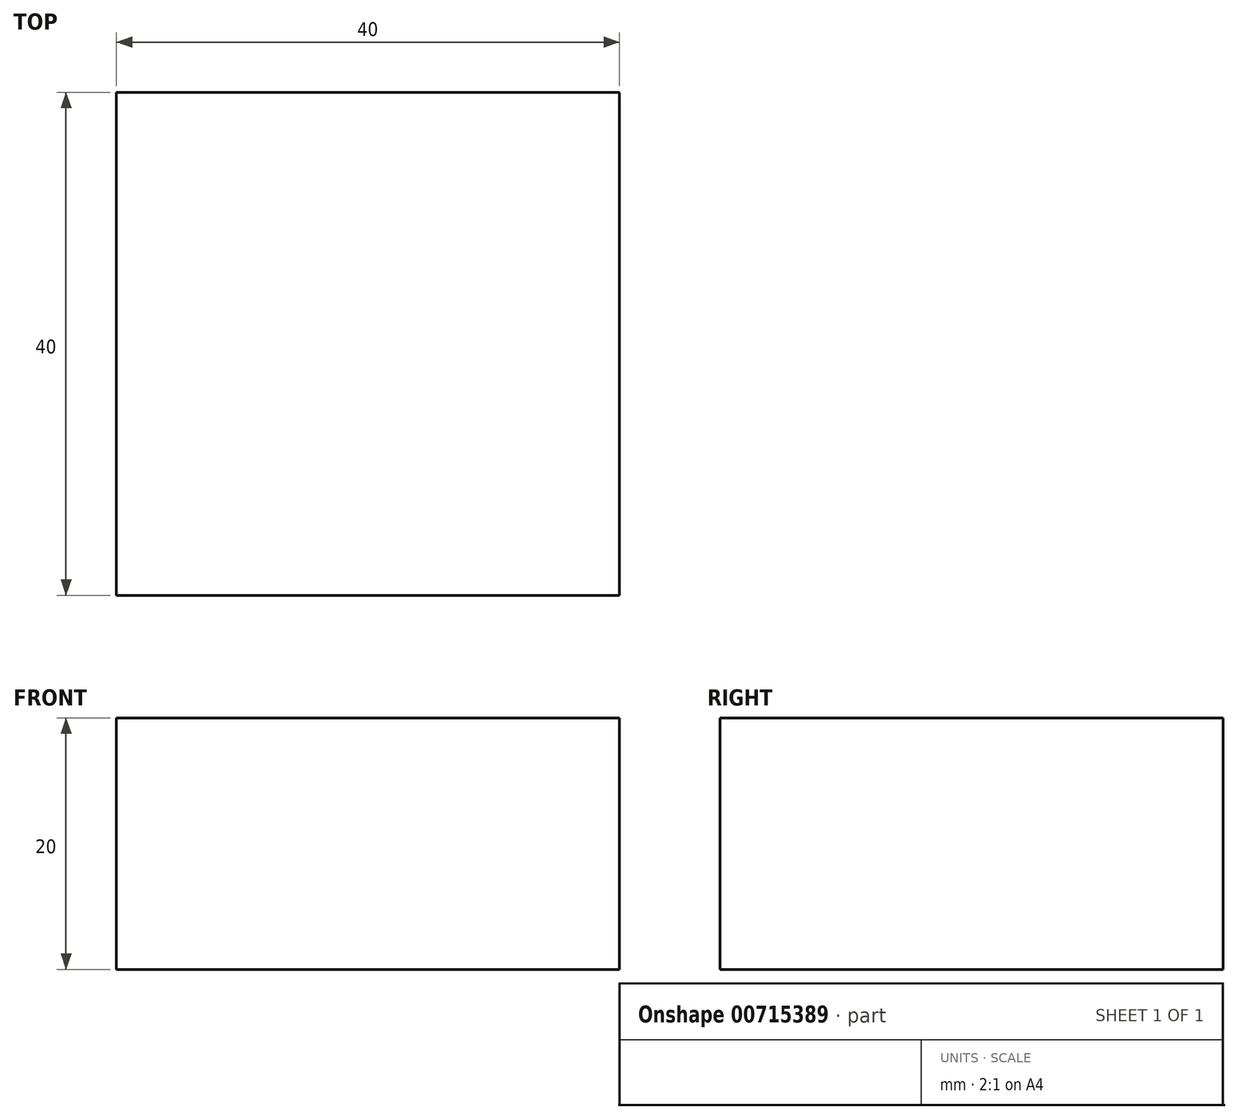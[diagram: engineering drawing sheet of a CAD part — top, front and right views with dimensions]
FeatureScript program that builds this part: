
annotation { "Feature Type Name" : "Feature", "Feature Type Description" : "" }
export const myFeature = defineFeature(function(context is Context, id is Id, definition is map)
    precondition{}
    {
        {
            var Q0;
            Q0=qCreatedBy(makeId("Front.planeOp"),FACE);
            var sketch = newSketch(context, id + "F0", { "sketchPlane" : qUnion([Q0])});
            skLineSegment(sketch, "E0.bottom", {"start": v(35, 20) * mm, "end": v(-35, 20) * mm});
            skLineSegment(sketch, "E0.top", {"start": v(35, -20) * mm, "end": v(-35, -20) * mm});
            skLineSegment(sketch, "E0.left", {"start": v(35, 20) * mm, "end": v(35, -20) * mm});
            skLineSegment(sketch, "E0.right", {"start": v(-35, 20) * mm, "end": v(-35, -20) * mm});
            skPoint(sketch, "E0.middle", {"position": v(0, 0) * mm});
            skLineSegment(sketch, "E1.bottom", {"start": v(35, 20) * mm, "end": v(-5, 20) * mm});
            skLineSegment(sketch, "E1.top", {"start": v(35, 0) * mm, "end": v(-5, 0) * mm});
            skLineSegment(sketch, "E1.left", {"start": v(35, 20) * mm, "end": v(35, 0) * mm});
            skLineSegment(sketch, "E1.right", {"start": v(-5, 20) * mm, "end": v(-5, 0) * mm});
            skSolve(sketch);
        }
        {
            var Q0;
            Q0=makeQuery(id+"F0.imprint","IMPRINT",FACE,{"disambiguationData":[TD([[makeQuery(id+"F0.imprint","IMPRINT",EDGE,{"derivedFrom":sQuery(id+"F0.wireOp",EDGE,"E0.bottom")}),1.0]])]});
            extrude(context, id + "F1", {"entities" : qUnion([Q0]), "depth" : 40 * mm, "offsetDistance" : 25 * mm});
        }
    });
